# Revit family: QF_BPRO_BLT 1020 EUK_572862
name_source: partatom
category: Sonderausstattung
revit_build: Autodesk Revit 2018 (Build: 20190510_1515(x64)
units: mm (PartAtom-declared; Revit-internal decimal feet)

## family parameters
Arbeitsebenenbasiert = Nein
Beim Laden mit Abzugskörper schneiden = Nein
Bemaßung runder Anschluss = Durchmesser verwenden
Gemeinsam genutzt = Nein
Immer vertikal = Ja
Raumberechnungspunkt = Ja
Teiletyp = Normal

## types (1)
- BLT 1020 EUK
    Artikel Nummer = 572862
    Beschreibung = B.PROTHERM 1020 EUK  Speisentransportbehälter, umluftgekühlt,
mit Flügeltür
Kapazität: GN-Behälter bis max. 3x GN 1/1-200 + 1x GN 1/1-100
Anzahl Auflagensicken: 14 Paar Auflagesicken
Sickenabstand: 57,5 mm
    Beschreibung durch Hersteller analog Leistungsverzeichniskurztext = Abmessungen

Länge:		                       540 mm
Breite:			845 mm
Höhe:			1.430 mm


Ausführung

Aufbau
Der Speisentransportbehälter besteht aus CNS 18/10, Werkstoff-Nr. 1.4301. Die Oberfläche ist mikroliert.  
Behälter und Flügeltür sind doppelwandig und mit FCKW-freiem PUR-Schaum temperaturisolierend ausgeschäumt. Der Behälter ist fahrbar mittels rostfreien Kunststoffrollen gemäß DIN 18867, Teil 8 (2 Bock- und 2 Lenkrollen mit Feststeller, Rollendurchmesser 125 mm). 
Die stabile Bodenkonstruktion aus Kunststoff mit integriertem, umlaufendem Stoßschutz schützt Gerät und Mobiliar vor Beschädigung.

Korpus
Die geschlossene Abdeckung des BLT 1020 EUK ist mit Stapelnoppen versehen, die die Stapelfähigkeit mit B.PROTHERM-Behältern aus Kunststoff ermöglichen.

Boden, Rück- und Seitenwände sind fugenlos verschweißt mit Kantradien R3 (Hygieneausführung H1). Die Seitenwände sind mit 14 Paar tiefgezogenen Auflagesicken im Abstand von 57,5 mm zur Aufnahme von Gastronorm-Behältern der Größe GN 1/1 oder deren Unterteilung versehen. An der Rückwand des Innenkorpus befinden sich - ebenfalls im Abstand von 57,5 mm - Prägungen, die auch bei Bestückung mit GN-Behältern ein Zirkulieren der Kaltluft und somit eine gleichmäßige Temperatur im Behälterinnenraum unterstützen.
Innenkorpus mit Außenkorpus frontseitig wasserdicht verschweißt.
An der Geräterückseite befindet sich der Spiralkabelanschluss mit Spiralkabel und Blindstecker-buchse.

Tür
Der Behälter ist frontseitig mit einer um 150° schwenkbaren, bei Bedarf abnehmbaren Flügeltür ausgestattet. Die Tür ist doppelwandig ausgeführt und mit FCKW-freiem PUR-Schaum temperaturisolierend ausgeschäumt.
Die Türinnenseite ist aus lebensmittelhygienisch unbedenklichem Polystyrol ausgeführt.
Das entnehmbare Luftleitblech aus CNS wird an der Türinnenseite eingehängt und sorgt für eine gleichmäßige horizontale und vertikale Verteilung der Kaltluft im Behälterinnenraum. Die Ausbrüche für die Luftansaug- und Luftausblasöffnung im unteren Drittel des Luftleitblechs sind mit je einem umlaufenden Dichtungsrahmen aus lebensmittelhygienisch unbedenklichem EPDM versehen.
Zusätzlich verfügt die Tür über einen umlaufenden herausnehmbaren Türdichtungsrahmen aus lebensmittelhygienisch unbedenklichem Silikon zur Minimierung von Kälteverlusten. 
Der eingeschäumte Türkontaktschalter sorgt dafür, dass die Kühlung beim Öffnen der Tür abschaltet – dadurch werden ein Vereisen des Verdampfers und unnötiger Energieverlust vermieden. 
Die Tür ist außen mit einer robustern Spannverschluss-leiste aus CNS versehen
Die Tür ist frontseitig mit einem CNS-Sicherheits-Schiebegriff mit seitlichen Stoßschutzelementen aus Kunststoff (Polyamid) ausgestattet. Der ergonomische Schiebegriff (Griffdurchmesser 32 mm) bietet zusätzliche Schutzfunktion.

Aktive Umluftkühlung
Die Kältemaschine befindet sich geschützt durch das Maschinengehäuse unterhalb des Korpus und oberhalb der Bodenplatte. 
Die Luftansaugung der Kältemaschine erfolgt seitlich und ist durch eine Revisionsblende mit Labyrinthführung vor Schmutzeintritt und Spritzwasser geschützt. Die Revisionsblende kann zu Reinigungszwecken leicht abgenommen werden.
Vor der Kältemaschine befinden sich der Lamellen-verdampfer und das Umluftgebläse, welches die Kaltluft aus dem Verdampfer über das in der Tür integrierte Luftleitblech gleichmäßig im Behälterinnenraum verteilt. Luftausblas- und Luftansaugöffnung sind durch ein zu Reinigungszwecken abnehmbares Schutzgitter geschützt. Am Schutzgitter ist rückseitig ein Kantprofil angebracht, das das Eindringen von Verunreinigungen erschwert.

Die aktive Umluftkühlung ist geeignet zum Kalthalten  von Speisen mit einer aus Hygienegründen geforderten maximalen Temperatur von +2°C bis +15°C. Die Temperatur ist durch einen digitalen Regler mit integriertem Ein-/ Ausschalter gradgenau regelbar. Der digitale Temperaturregler ist benutzerfreundlich im Korpusdach integriert.

Bodenkonstruktion
Stabile, geschlossene Bodenkonstruktion aus massivem Kunststoff mit integriertem, umlaufendem Stoßschutz. An der Unterseite sind Profile aus CNS zur Aufnahme der Tauwasserauffangschale (GN 1/3-40) angebracht.

Alle Verschleißteile (wie z.B. Rollen, Schiebegriff, Verschlüsse etc.) sind im Servicefall einfach austauschbar. 



Zubehör/ Optionen

•	Zusätzlicher Stoßschutz am Dach aus massivem Kunststoff (analog Bodenplatte)
•	Dach (glatt) mit umlaufender Galerie aus CNS
•	220-240 V/ 60Hz-Variante
•	Zusätzlicher Schiebegriff an der Geräterückseite
•	Tür nicht aushängbar
•	Eutektische Platte -3°C, aus Kunststoff (Best.Nr. 568 136)
•	Eutektische Platte -12°C, aus Kunststoff (Best.Nr. 573 332)
•	Einschubrahmen zur Unterteilung von GN-Behältern mit max. Tiefe 150 mm  (Best.Nr. 564 352)
•	GN-Stege zum variablen Einsetzen von GN-Behältern der Größe GN 1/4, GN 1/6, GN 1/9 in den Einschubrahmen (ST 3 Best.Nr. 550 650, 
ST 5 Best.Nr. 550 651)
•	Menükarten-Halterung an Tür frontseitig zur Aufnahme von Menükarten DIN A 6
•	BLT E-Menükarte mit Schlüssellochung, DIN A 6 (Best.Nr. 572 513) 
•	Spezialstift, zur Beschriftung der BLT E-Menükarten                (Best.Nr. 564 361)
•	Menükarten-Box, Kunststoff (Best.Nr. 564 355)
•	Weitere Rollenoptionen siehe Gesamtpreisliste



 
Technische Daten

Werkstoff:	Chromnickelstahl 18/10,
	                        Kunststoff
Isoliermaterial:	PUR-Schaum, FCKW-frei 
Gewicht:	                        97 kg
Kapazität:	max. 3x GN 1/1-200 + 1x GN 
	                        1/1-100 oder 14x GN 1/1-55
Sicken:	                       14 Paar tiefgezogene Auflagesicken, 
	                        Sickenabstand 57,5 mm
Temperaturbereich:	von +2°C bis +15°C gradgenau regelbar bei einer Umgebungstemperatur von +32°C
Kältemittel:	R134a
Kälteleistung:	0,37kW bei t0= -10°C und tu= +32°C
Anschlusswert:	220-240V AC/ 50Hz/ 0,3kW
Emissionen:	Der arbeitsplatzbezogene 
	                        Schallpegel des Geräts ist
	                        kleiner als 70 dB(A)



Besonderheit

•	aktive Umluftkühlung
•	wasserdichter Innenkorpus in Hygieneausführung H1, Kantradien R3
•	Türkontaktschalter
•	Schutzart IP X4 (Schutz gegen Spritzwasser)
•	geeignet für Energie-Optimierungsanlagen



Fabrikat

Hersteller:   B.PRO
Modell:	     BLT 1020 EUK
	     B.PROTHERM
Best. Nr.	     572 862
    Beschreibung durch Hersteller analog Leistungsverzeichnislangtext = Abmessungen

Länge:		                       540 mm
Breite:			845 mm
Höhe:			1.430 mm


Ausführung

Aufbau
Der Speisentransportbehälter besteht aus CNS 18/10, Werkstoff-Nr. 1.4301. Die Oberfläche ist mikroliert.  
Behälter und Flügeltür sind doppelwandig und mit FCKW-freiem PUR-Schaum temperaturisolierend ausgeschäumt. Der Behälter ist fahrbar mittels rostfreien Kunststoffrollen gemäß DIN 18867, Teil 8 (2 Bock- und 2 Lenkrollen mit Feststeller, Rollendurchmesser 125 mm). 
Die stabile Bodenkonstruktion aus Kunststoff mit integriertem, umlaufendem Stoßschutz schützt Gerät und Mobiliar vor Beschädigung.

Korpus
Die geschlossene Abdeckung des BLT 1020 EUK ist mit Stapelnoppen versehen, die die Stapelfähigkeit mit B.PROTHERM-Behältern aus Kunststoff ermöglichen.

Boden, Rück- und Seitenwände sind fugenlos verschweißt mit Kantradien R3 (Hygieneausführung H1). Die Seitenwände sind mit 14 Paar tiefgezogenen Auflagesicken im Abstand von 57,5 mm zur Aufnahme von Gastronorm-Behältern der Größe GN 1/1 oder deren Unterteilung versehen. An der Rückwand des Innenkorpus befinden sich - ebenfalls im Abstand von 57,5 mm - Prägungen, die auch bei Bestückung mit GN-Behältern ein Zirkulieren der Kaltluft und somit eine gleichmäßige Temperatur im Behälterinnenraum unterstützen.
Innenkorpus mit Außenkorpus frontseitig wasserdicht verschweißt.
An der Geräterückseite befindet sich der Spiralkabelanschluss mit Spiralkabel und Blindstecker-buchse.

Tür
Der Behälter ist frontseitig mit einer um 150° schwenkbaren, bei Bedarf abnehmbaren Flügeltür ausgestattet. Die Tür ist doppelwandig ausgeführt und mit FCKW-freiem PUR-Schaum temperaturisolierend ausgeschäumt.
Die Türinnenseite ist aus lebensmittelhygienisch unbedenklichem Polystyrol ausgeführt.
Das entnehmbare Luftleitblech aus CNS wird an der Türinnenseite eingehängt und sorgt für eine gleichmäßige horizontale und vertikale Verteilung der Kaltluft im Behälterinnenraum. Die Ausbrüche für die Luftansaug- und Luftausblasöffnung im unteren Drittel des Luftleitblechs sind mit je einem umlaufenden Dichtungsrahmen aus lebensmittelhygienisch unbedenklichem EPDM versehen.
Zusätzlich verfügt die Tür über einen umlaufenden herausnehmbaren Türdichtungsrahmen aus lebensmittelhygienisch unbedenklichem Silikon zur Minimierung von Kälteverlusten. 
Der eingeschäumte Türkontaktschalter sorgt dafür, dass die Kühlung beim Öffnen der Tür abschaltet – dadurch werden ein Vereisen des Verdampfers und unnötiger Energieverlust vermieden. 
Die Tür ist außen mit einer robustern Spannverschluss-leiste aus CNS versehen
Die Tür ist frontseitig mit einem CNS-Sicherheits-Schiebegriff mit seitlichen Stoßschutzelementen aus Kunststoff (Polyamid) ausgestattet. Der ergonomische Schiebegriff (Griffdurchmesser 32 mm) bietet zusätzliche Schutzfunktion.

Aktive Umluftkühlung
Die Kältemaschine befindet sich geschützt durch das Maschinengehäuse unterhalb des Korpus und oberhalb der Bodenplatte. 
Die Luftansaugung der Kältemaschine erfolgt seitlich und ist durch eine Revisionsblende mit Labyrinthführung vor Schmutzeintritt und Spritzwasser geschützt. Die Revisionsblende kann zu Reinigungszwecken leicht abgenommen werden.
Vor der Kältemaschine befinden sich der Lamellen-verdampfer und das Umluftgebläse, welches die Kaltluft aus dem Verdampfer über das in der Tür integrierte Luftleitblech gleichmäßig im Behälterinnenraum verteilt. Luftausblas- und Luftansaugöffnung sind durch ein zu Reinigungszwecken abnehmbares Schutzgitter geschützt. Am Schutzgitter ist rückseitig ein Kantprofil angebracht, das das Eindringen von Verunreinigungen erschwert.

Die aktive Umluftkühlung ist geeignet zum Kalthalten  von Speisen mit einer aus Hygienegründen geforderten maximalen Temperatur von +2°C bis +15°C. Die Temperatur ist durch einen digitalen Regler mit integriertem Ein-/ Ausschalter gradgenau regelbar. Der digitale Temperaturregler ist benutzerfreundlich im Korpusdach integriert.

Bodenkonstruktion
Stabile, geschlossene Bodenkonstruktion aus massivem Kunststoff mit integriertem, umlaufendem Stoßschutz. An der Unterseite sind Profile aus CNS zur Aufnahme der Tauwasserauffangschale (GN 1/3-40) angebracht.

Alle Verschleißteile (wie z.B. Rollen, Schiebegriff, Verschlüsse etc.) sind im Servicefall einfach austauschbar. 



Zubehör/ Optionen

•	Zusätzlicher Stoßschutz am Dach aus massivem Kunststoff (analog Bodenplatte)
•	Dach (glatt) mit umlaufender Galerie aus CNS
•	220-240 V/ 60Hz-Variante
•	Zusätzlicher Schiebegriff an der Geräterückseite
•	Tür nicht aushängbar
•	Eutektische Platte -3°C, aus Kunststoff (Best.Nr. 568 136)
•	Eutektische Platte -12°C, aus Kunststoff (Best.Nr. 573 332)
•	Einschubrahmen zur Unterteilung von GN-Behältern mit max. Tiefe 150 mm  (Best.Nr. 564 352)
•	GN-Stege zum variablen Einsetzen von GN-Behältern der Größe GN 1/4, GN 1/6, GN 1/9 in den Einschubrahmen (ST 3 Best.Nr. 550 650, 
ST 5 Best.Nr. 550 651)
•	Menükarten-Halterung an Tür frontseitig zur Aufnahme von Menükarten DIN A 6
•	BLT E-Menükarte mit Schlüssellochung, DIN A 6 (Best.Nr. 572 513) 
•	Spezialstift, zur Beschriftung der BLT E-Menükarten                (Best.Nr. 564 361)
•	Menükarten-Box, Kunststoff (Best.Nr. 564 355)
•	Weitere Rollenoptionen siehe Gesamtpreisliste



 
Technische Daten

Werkstoff:	Chromnickelstahl 18/10,
	                        Kunststoff
Isoliermaterial:	PUR-Schaum, FCKW-frei 
Gewicht:	                        97 kg
Kapazität:	max. 3x GN 1/1-200 + 1x GN 
	                        1/1-100 oder 14x GN 1/1-55
Sicken:	                       14 Paar tiefgezogene Auflagesicken, 
	                        Sickenabstand 57,5 mm
Temperaturbereich:	von +2°C bis +15°C gradgenau regelbar bei einer Umgebungstemperatur von +32°C
Kältemittel:	R134a
Kälteleistung:	0,37kW bei t0= -10°C und tu= +32°C
Anschlusswert:	220-240V AC/ 50Hz/ 0,3kW
Emissionen:	Der arbeitsplatzbezogene 
	                        Schallpegel des Geräts ist
	                        kleiner als 70 dB(A)



Besonderheit

•	aktive Umluftkühlung
•	wasserdichter Innenkorpus in Hygieneausführung H1, Kantradien R3
•	Türkontaktschalter
•	Schutzart IP X4 (Schutz gegen Spritzwasser)
•	geeignet für Energie-Optimierungsanlagen



Fabrikat

Hersteller:   B.PRO
Modell:	     BLT 1020 EUK
	     B.PROTHERM
Best. Nr.	     572 862
    CE Kennzeichnung = Ja
    Elektrische leistung = 300 W
    Frequenz = 50 Hz
    Gerätegewicht Netto = 96.40 kg
    Großküchengerätezuordnung = Ja
    Hauptschalter integriert = Ja
    Hersteller = B.PRO GmbH
    Höhe = 1434 mm  [stored 4.70472 ft]
    Internetadresse Gerätehersteller = https://www.bpro-solutions.com
    Internetadresse für Ersatzteilliste = https://www.bpro-solutions.com
    Kosten = 6815.7 $
    Länge Gerätebreite = 540 mm  [stored 1.77165 ft]
    Material = <Nach Kategorie>
    Modell = BLT 1020 EUK
    Schalldruckpegel = < 70 dB(A)
    Spannung = 220 V
    Stecker System = Schuko Stecker
    Tiefe = 845 mm  [stored 2.77231 ft]
    Typenkommentare = Speisetransportbehälter gekühlt
    URL = https://www.bpro-solutions.com
    Warnhinweise = Aufrechte Transportposition:
Gerät nur aufrecht stehend transportieren.
Wenn das Gerät nicht aufrecht stehend transportiert wurde, mit der Inbetriebnahme 2 Stunden warten.

Transport mit LKW oder Lieferwagen:
Gerät nur in LKW oder Lieferwagen mit Laderampe transportieren. Die Laderampe darf einen Neigungswinkel von 10° nicht überschreiten.
Gerät von allen vier Seiten gegen Verrutschen sichern.
Gerät gegen vertikale Bewegungen während des Transports sichern.
Gepolsterte Sicherungsstangen einsetzen.
Eine Transportsicherung nur mit den Feststellbremsen ist nicht ausreichend.

Standort:
Gerät nie neben Geräten mit starker Dampfentwicklung betreiben (z. B. Spülmaschine). Die Dämpfe können zur Betauung des Geräts führen.
Durch den Feuchtigkeitsfilm entsteht bei angeschlossenem Gerät die Gefahr
eines Kurzschlusses oder eines elektrischen Schlags.
Lüftungsschlitze des Kühlaggregats freihalten. Lüftungsschlitze müssen bei
eingeschaltetem Kühlaggregat mindestens 10 cm Abstand zu einer Wand
haben. Zugestellte Lüftungsschlitze können zur Überhitzung und zum Ausfall
des Kühlaggregats führen.

Beschickung:
Um eine Verlagerung des Schwerpunkts zur Geräteoberseite zu vermeiden,
Gerät bei Teilbeschickung von unten nach oben beschicken.

Ausführliche Gefahrenhinweise entnehmen Sie der Betriebsanleitung.
    Zubehör = Ja
    Zuleitung zum Gerät im Lieferumfang = Ja

note: [stored X ft] marks values corroborated as IEEE doubles in the binary element streams (Revit-internal decimal feet)
